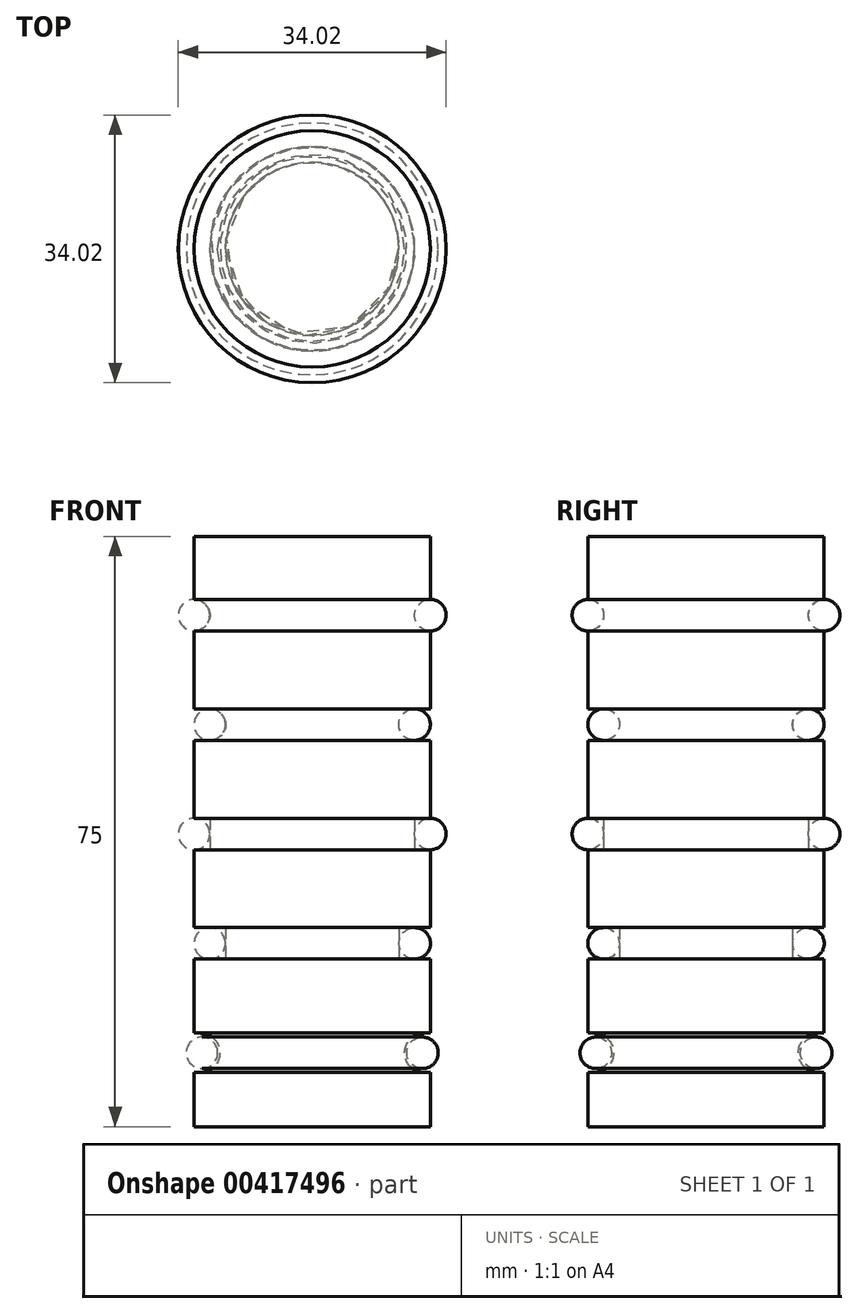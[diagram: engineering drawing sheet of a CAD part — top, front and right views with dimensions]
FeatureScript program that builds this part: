
annotation { "Feature Type Name" : "Feature", "Feature Type Description" : "" }
export const myFeature = defineFeature(function(context is Context, id is Id, definition is map)
    precondition{}
    {
        {
            var Q0;
            Q0=qCreatedBy(makeId("Front.planeOp"),FACE);
            var sketch = newSketch(context, id + "F0", { "sketchPlane" : qUnion([Q0])});
            skLineSegment(sketch, "E0.bottom", {"start": v(15, -30) * mm, "end": v(0, -30) * mm});
            skLineSegment(sketch, "E0.top", {"start": v(15, 45) * mm, "end": v(0, 45) * mm});
            skLineSegment(sketch, "E0.left", {"start": v(15, -30) * mm, "end": v(15, 45) * mm});
            skLineSegment(sketch, "E0.right", {"start": v(0, -30) * mm, "end": v(0, 45) * mm});
            skPoint(sketch, "E0.middle", {"position": v(7.5, 7.5) * mm});
            skSolve(sketch);
        }
        {
            var Q0;
            Q0=makeQuery(id+"F0.imprint","IMPRINT",FACE,{"disambiguationData":[TD([[makeQuery(id+"F0.imprint","IMPRINT",EDGE,{"derivedFrom":sQuery(id+"F0.wireOp",EDGE,"E0.bottom")}),-1.0]])]});
            var Q1;
            {var subQ0=sQuery(id+"F0.wireOp",EDGE,"5e272fc4-2224-443f-91dc-8f4b177eb3e2.2.0.0");Q1=makeQuery(id+"F0.imprint","IMPRINT",FACE,{"disambiguationData":[TD([[makeQuery(id+"F0.imprint","IMPRINT",EDGE,{"derivedFrom":subQ0}),-1.0]])]});}
            var Q2;
            {var subQ0=sQuery(id+"F0.wireOp",EDGE,"5e272fc4-2224-443f-91dc-8f4b177eb3e2.1.0.0");Q2=makeQuery(id+"F0.imprint","IMPRINT",FACE,{"disambiguationData":[TD([[makeQuery(id+"F0.imprint","IMPRINT",EDGE,{"derivedFrom":subQ0}),-1.0]])]});}
            var Q3;
            {var subQ0=sQuery(id+"F0.wireOp",EDGE,"QAZxaHZ0-HoTb-1XEE-ymKS-uFKnrcYPTaCr");Q3=makeQuery(id+"F0.imprint","IMPRINT",FACE,{"disambiguationData":[TD([[makeQuery(id+"F0.imprint","IMPRINT",EDGE,{"derivedFrom":subQ0}),-1.0]])]});}
            var Q4;
            {var subQ0=sQuery(id+"F0.wireOp",EDGE,"E0.top");Q4=makeQuery(id+"F0.imprint","IMPRINT",FACE,{"disambiguationData":[TD([[makeQuery(id+"F0.imprint","IMPRINT",EDGE,{"derivedFrom":subQ0}),1.0]])]});}
            var Q5;
            Q5=sQuery(id+"F0.wireOp",EDGE,"E0.right");
            revolve(context, id + "F1", {"entities" : qUnion([Q0, Q1, Q2, Q3, Q4]), "axis" : qUnion([Q5]), "revolveType" : RevolveType.FULL});
        }
        {
            var Q0;
            Q0=qCreatedBy(makeId("Front.planeOp"),FACE);
            var sketch = newSketch(context, id + "F2", { "sketchPlane" : qUnion([Q0])});
            skPoint(sketch, "E1.middle", {"position": v(7.5, 0) * mm});
            skLineSegment(sketch, "E2", {"start": v(0, 34.98) * mm, "end": v(15, 34.98) * mm});
            skLineSegment(sketch, "E3.1.0.0", {"start": v(0, 21.08) * mm, "end": v(15, 21.08) * mm});
            skLineSegment(sketch, "E3.2.0.0", {"start": v(0, 7.18) * mm, "end": v(15, 7.18) * mm});
            skLineSegment(sketch, "E3.3.0.0", {"start": v(0, -6.72) * mm, "end": v(15, -6.72) * mm});
            skLineSegment(sketch, "E3.direction1", {"start": v(0, 34.98) * mm, "end": v(0, 21.08) * mm, "construction": true});
            skPoint(sketch, "E4", {"position": v(15, 21.08) * mm});
            skLineSegment(sketch, "E5.0.4.0", {"start": v(0, -20.62) * mm, "end": v(15, -20.62) * mm});
            skSolve(sketch);
        }
        {
            var Q0;
            Q0=sQuery(id+"F2.wireOp",EDGE,"E2");
            var Q1;
            Q1=sQuery(id+"F2.wireOp",EDGE,"E3.1.0.0");
            var Q2;
            Q2=sQuery(id+"F2.wireOp",EDGE,"E3.2.0.0");
            var Q3;
            Q3=sQuery(id+"F2.wireOp",EDGE,"E3.3.0.0");
            var Q4;
            Q4=sQuery(id+"F2.wireOp",EDGE,"E5.0.4.0");
            var Q5;
            Q5=sQuery(id+"F2.wireOp",EDGE,"E3.direction1");
            revolve(context, id + "F3", {"bodyType" : ToolBodyType.SURFACE, "surfaceEntities" : qUnion([Q0, Q1, Q2, Q3, Q4]), "axis" : qUnion([Q5]), "revolveType" : RevolveType.FULL});
        }
        {
            var Q0;
            Q0=qCreatedBy(makeId("Front.planeOp"),FACE);
            var sketch = newSketch(context, id + "F4", { "sketchPlane" : qUnion([Q0])});
            skCircle(sketch, "E6", {"center": v(15, 34.98) * mm, "radius": 2 * mm});
            skSolve(sketch);
        }
        {
            var Q0;
            Q0 = qSketchRegion(id + "F4", true);
            var Q1;
            Q1=makeQuery(id+"F3.opRevolve","SWEPT_EDGE",EDGE,{"disambiguationData":[OSD([sQuery(id+"F2.wireOp",VERTEX,"E2.end")])]});
            sweep(context, id + "F5", {"operationType" : NewBodyOperationType.REMOVE, "profiles" : qUnion([Q0]), "path" : qUnion([Q1])});
        }
        {
            var Q0;
            Q0=qCreatedBy(makeId("Front.planeOp"),FACE);
            var sketch = newSketch(context, id + "F6", { "sketchPlane" : qUnion([Q0])});
            skLineSegment(sketch, "E7.bottom", {"start": v(17, 19.08) * mm, "end": v(13, 19.08) * mm});
            skLineSegment(sketch, "E7.top", {"start": v(17, 23.08) * mm, "end": v(13, 23.08) * mm});
            skLineSegment(sketch, "E7.left", {"start": v(17, 19.08) * mm, "end": v(17, 23.08) * mm});
            skLineSegment(sketch, "E7.right", {"start": v(13, 19.08) * mm, "end": v(13, 23.08) * mm});
            skPoint(sketch, "E7.middle", {"position": v(15, 21.08) * mm});
            skCircle(sketch, "E8", {"center": v(13, 21.08) * mm, "radius": 2 * mm});
            skLineSegment(sketch, "E9.bottom", {"start": v(9.57, 733.78) * mm, "end": v(5.57, 733.78) * mm});
            skLineSegment(sketch, "E9.top", {"start": v(9.57, 737.78) * mm, "end": v(5.57, 737.78) * mm});
            skLineSegment(sketch, "E9.left", {"start": v(9.57, 733.78) * mm, "end": v(9.57, 737.78) * mm});
            skLineSegment(sketch, "E9.right", {"start": v(5.57, 733.78) * mm, "end": v(5.57, 737.78) * mm});
            skPoint(sketch, "E9.middle", {"position": v(7.57, 735.78) * mm});
            skCircle(sketch, "E10", {"center": v(5.57, 735.78) * mm, "radius": 2 * mm});
            skSolve(sketch);
        }
        {
            var Q0;
            Q0 = qSketchRegion(id + "F6", true);
            var Q1;
            Q1=makeQuery(id+"F3.opRevolve","SWEPT_EDGE",EDGE,{"disambiguationData":[OSD([sQuery(id+"F2.wireOp",VERTEX,"E3.1.0.0.end")])]});
            sweep(context, id + "F7", {"operationType" : NewBodyOperationType.REMOVE, "profiles" : qUnion([Q0]), "path" : qUnion([Q1])});
        }
        {
            var Q0;
            Q0=qCreatedBy(makeId("Front.planeOp"),FACE);
            var sketch = newSketch(context, id + "F8", { "sketchPlane" : qUnion([Q0])});
            skLineSegment(sketch, "E11.bottom", {"start": v(17, 5.18) * mm, "end": v(13, 5.18) * mm});
            skLineSegment(sketch, "E11.top", {"start": v(17, 9.18) * mm, "end": v(13, 9.18) * mm});
            skLineSegment(sketch, "E11.left", {"start": v(17, 5.18) * mm, "end": v(17, 9.18) * mm});
            skLineSegment(sketch, "E11.right", {"start": v(13, 5.18) * mm, "end": v(13, 9.18) * mm});
            skPoint(sketch, "E11.middle", {"position": v(15, 7.18) * mm});
            skSolve(sketch);
        }
        {
            var Q0;
            Q0=makeQuery(id+"F8.imprint","IMPRINT",FACE,{"disambiguationData":[TD([[makeQuery(id+"F8.imprint","IMPRINT",EDGE,{"derivedFrom":sQuery(id+"F8.wireOp",EDGE,"E11.bottom")}),-1.0]])]});
            var Q1;
            Q1=makeQuery(id+"F3.opRevolve","SWEPT_EDGE",EDGE,{"disambiguationData":[OSD([sQuery(id+"F2.wireOp",VERTEX,"E3.2.0.0.end")])]});
            sweep(context, id + "F9", {"operationType" : NewBodyOperationType.REMOVE, "profiles" : qUnion([Q0]), "path" : qUnion([Q1])});
        }
        {
            var Q0;
            Q0=qCreatedBy(makeId("Front.planeOp"),FACE);
            var sketch = newSketch(context, id + "F10", { "sketchPlane" : qUnion([Q0])});
            skLineSegment(sketch, "E12.bottom", {"start": v(15, -8.72) * mm, "end": v(11, -8.72) * mm});
            skLineSegment(sketch, "E12.top", {"start": v(15, -4.72) * mm, "end": v(11, -4.72) * mm});
            skLineSegment(sketch, "E12.left", {"start": v(15, -8.72) * mm, "end": v(15, -4.72) * mm});
            skLineSegment(sketch, "E12.right", {"start": v(11, -8.72) * mm, "end": v(11, -4.72) * mm});
            skPoint(sketch, "E12.middle", {"position": v(13, -6.72) * mm});
            skSolve(sketch);
        }
        {
            var Q0;
            Q0 = qSketchRegion(id + "F10", true);
            var Q1;
            Q1=makeQuery(id+"F3.opRevolve","SWEPT_EDGE",EDGE,{"disambiguationData":[OSD([sQuery(id+"F2.wireOp",VERTEX,"E3.3.0.0.end")])]});
            sweep(context, id + "F11", {"operationType" : NewBodyOperationType.REMOVE, "profiles" : qUnion([Q0]), "path" : qUnion([Q1])});
        }
        {
            var Q0;
            Q0=qCreatedBy(makeId("Front.planeOp"),FACE);
            var sketch = newSketch(context, id + "F12", { "sketchPlane" : qUnion([Q0])});
            skLineSegment(sketch, "E13.bottom", {"start": v(18.24, -23.12) * mm, "end": v(14.24, -23.12) * mm});
            skLineSegment(sketch, "E13.top", {"start": v(18.24, -18.12) * mm, "end": v(14.24, -18.12) * mm});
            skLineSegment(sketch, "E13.left", {"start": v(18.24, -23.12) * mm, "end": v(18.24, -18.12) * mm});
            skLineSegment(sketch, "E13.right", {"start": v(14.24, -23.12) * mm, "end": v(14.24, -18.12) * mm});
            skPoint(sketch, "E13.middle", {"position": v(16.24, -20.62) * mm});
            skCircle(sketch, "E14", {"center": v(14.24, -20.62) * mm, "radius": 2.5 * mm});
            skSolve(sketch);
        }
        {
            var Q0;
            Q0 = qSketchRegion(id + "F12", true);
            var Q1;
            Q1=makeQuery(id+"F3.opRevolve","SWEPT_EDGE",EDGE,{"disambiguationData":[OSD([sQuery(id+"F2.wireOp",VERTEX,"E5.0.4.0.end")])]});
            sweep(context, id + "F13", {"operationType" : NewBodyOperationType.REMOVE, "profiles" : qUnion([Q0]), "path" : qUnion([Q1])});
        }
        {
            var Q0;
            Q0=qCreatedBy(makeId("Front.planeOp"),FACE);
            var sketch = newSketch(context, id + "F14", { "sketchPlane" : qUnion([Q0])});
            skCircle(sketch, "E15", {"center": v(14, -20.62) * mm, "radius": 2 * mm});
            skCircle(sketch, "E16", {"center": v(13.02, -6.72) * mm, "radius": 2 * mm});
            skCircle(sketch, "E17", {"center": v(15, 7.18) * mm, "radius": 2 * mm});
            skCircle(sketch, "E18", {"center": v(13, 21.08) * mm, "radius": 2 * mm});
            skCircle(sketch, "E19", {"center": v(15, 34.98) * mm, "radius": 2 * mm});
            skSolve(sketch);
        }
        {
            var Q0;
            Q0=makeQuery(id+"F14.imprint","IMPRINT",FACE,{"disambiguationData":[TD([[makeQuery(id+"F14.imprint","IMPRINT",EDGE,{"derivedFrom":sQuery(id+"F14.wireOp",EDGE,"E19")}),1.0]])]});
            var Q1;
            Q1=makeQuery(id+"F14.imprint","IMPRINT",FACE,{"disambiguationData":[TD([[makeQuery(id+"F14.imprint","IMPRINT",EDGE,{"derivedFrom":sQuery(id+"F14.wireOp",EDGE,"E18")}),1.0]])]});
            var Q2;
            Q2=makeQuery(id+"F14.imprint","IMPRINT",FACE,{"disambiguationData":[TD([[makeQuery(id+"F14.imprint","IMPRINT",EDGE,{"derivedFrom":sQuery(id+"F14.wireOp",EDGE,"E17")}),1.0]])]});
            var Q3;
            Q3=makeQuery(id+"F14.imprint","IMPRINT",FACE,{"disambiguationData":[TD([[makeQuery(id+"F14.imprint","IMPRINT",EDGE,{"derivedFrom":sQuery(id+"F14.wireOp",EDGE,"E16")}),1.0]])]});
            var Q4;
            Q4=makeQuery(id+"F14.imprint","IMPRINT",FACE,{"disambiguationData":[TD([[makeQuery(id+"F14.imprint","IMPRINT",EDGE,{"derivedFrom":sQuery(id+"F14.wireOp",EDGE,"E15")}),1.0]])]});
            var Q5;
            Q5=makeQuery(id+"F3.opRevolve","SWEPT_EDGE",EDGE,{"disambiguationData":[OSD([sQuery(id+"F2.wireOp",VERTEX,"E2.end")])]});
            sweep(context, id + "F15", {"profiles" : qUnion([Q0, Q1, Q2, Q3, Q4]), "path" : qUnion([Q5])});
        }
    });
